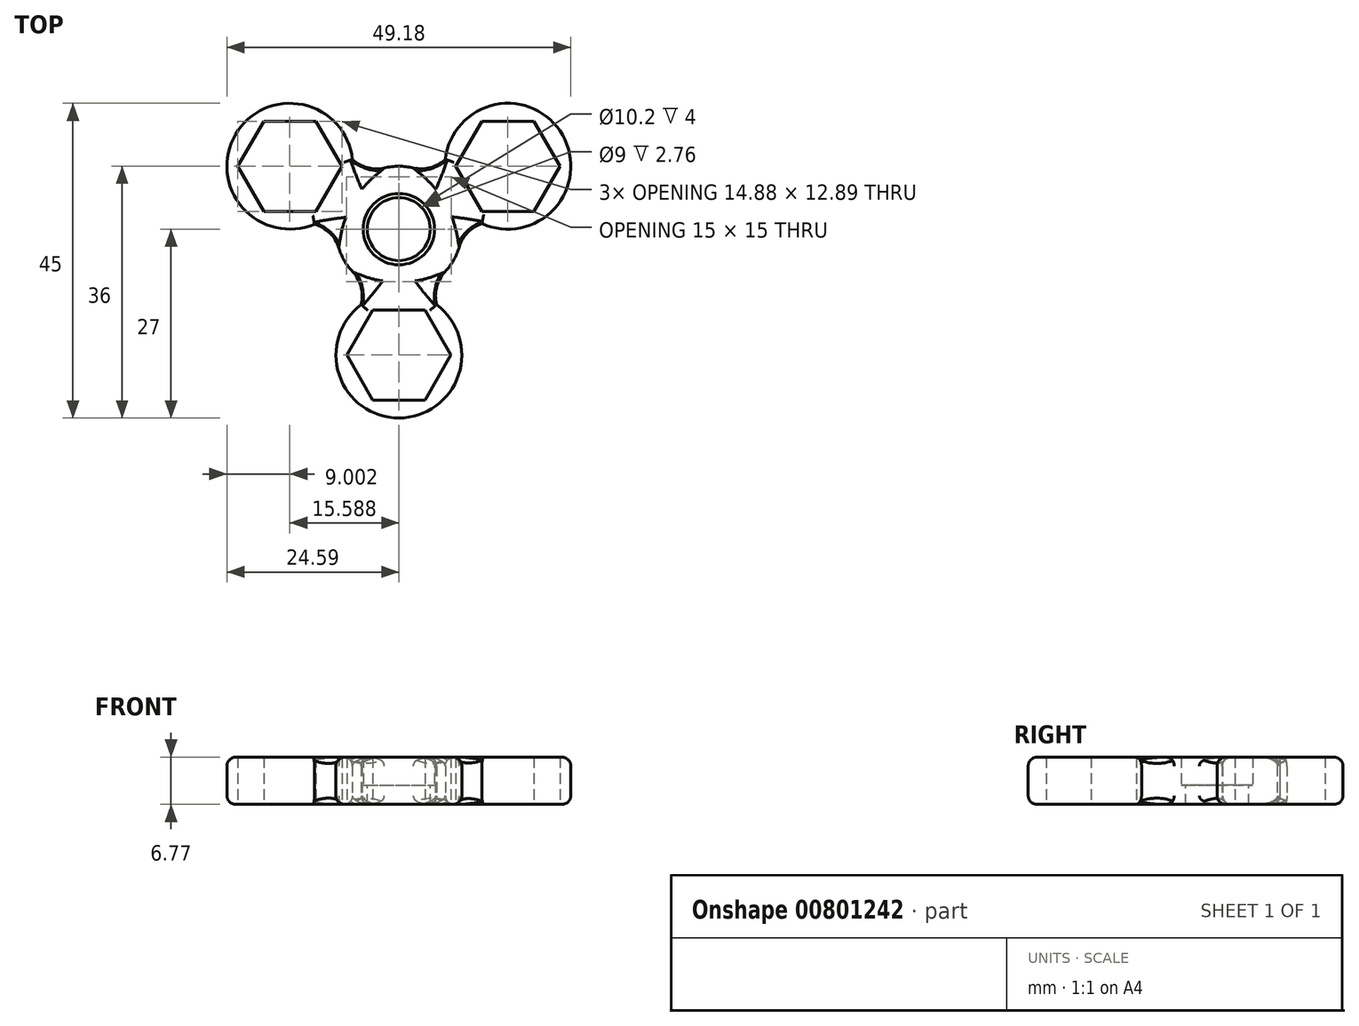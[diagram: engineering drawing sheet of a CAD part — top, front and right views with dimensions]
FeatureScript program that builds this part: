
annotation { "Feature Type Name" : "Feature", "Feature Type Description" : "" }
export const myFeature = defineFeature(function(context is Context, id is Id, definition is map)
    precondition{}
    {
        {
            var Q0;
            Q0=qCreatedBy(makeId("Top.planeOp"),FACE);
            var sketch = newSketch(context, id + "F0", { "sketchPlane" : qUnion([Q0])});
            skCircle(sketch, "E0.cCircle", {"center": v(0, 0) * mm, "radius": 9 * mm, "construction": true});
            skPoint(sketch, "E0.0.midPoint", {"position": v(0, 9) * mm});
            skCircle(sketch, "E1.cCircle", {"center": v(-15.59, 9) * mm, "radius": 6.44 * mm, "construction": true});
            skLineSegment(sketch, "E1.0", {"start": v(-19.3, 15.45) * mm, "end": v(-11.87, 15.45) * mm});
            skLineSegment(sketch, "E1.1", {"start": v(-11.87, 15.45) * mm, "end": v(-8.15, 9) * mm});
            skLineSegment(sketch, "E1.2", {"start": v(-8.15, 9) * mm, "end": v(-11.87, 2.55) * mm});
            skLineSegment(sketch, "E1.3", {"start": v(-11.87, 2.56) * mm, "end": v(-19.3, 2.56) * mm});
            skLineSegment(sketch, "E1.4", {"start": v(-19.3, 2.55) * mm, "end": v(-23.03, 9) * mm});
            skLineSegment(sketch, "E1.5", {"start": v(-23.03, 9) * mm, "end": v(-19.3, 15.45) * mm});
            skPoint(sketch, "E1.0.midPoint", {"position": v(-15.59, 15.45) * mm});
            skCircle(sketch, "E2.cCircle", {"center": v(15.59, 9) * mm, "radius": 6.44 * mm, "construction": true});
            skLineSegment(sketch, "E2.0", {"start": v(11.87, 2.55) * mm, "end": v(8.15, 9) * mm});
            skLineSegment(sketch, "E2.1", {"start": v(8.15, 9) * mm, "end": v(11.87, 15.45) * mm});
            skLineSegment(sketch, "E2.2", {"start": v(11.87, 15.45) * mm, "end": v(19.3, 15.45) * mm});
            skLineSegment(sketch, "E2.3", {"start": v(19.3, 15.45) * mm, "end": v(23.03, 9) * mm});
            skLineSegment(sketch, "E2.4", {"start": v(23.03, 9) * mm, "end": v(19.3, 2.56) * mm});
            skLineSegment(sketch, "E2.5", {"start": v(19.3, 2.56) * mm, "end": v(11.87, 2.55) * mm});
            skPoint(sketch, "E2.0.midPoint", {"position": v(10, 5.78) * mm});
            skCircle(sketch, "E3.cCircle", {"center": v(0, -18) * mm, "radius": 6.45 * mm, "construction": true});
            skLineSegment(sketch, "E3.0", {"start": v(-3.72, -11.56) * mm, "end": v(3.72, -11.56) * mm});
            skLineSegment(sketch, "E3.1", {"start": v(3.72, -11.55) * mm, "end": v(7.44, -18) * mm});
            skLineSegment(sketch, "E3.2", {"start": v(7.44, -18) * mm, "end": v(3.72, -24.44) * mm});
            skLineSegment(sketch, "E3.3", {"start": v(3.72, -24.45) * mm, "end": v(-3.72, -24.45) * mm});
            skLineSegment(sketch, "E3.4", {"start": v(-3.72, -24.45) * mm, "end": v(-7.44, -18) * mm});
            skLineSegment(sketch, "E3.5", {"start": v(-7.44, -18) * mm, "end": v(-3.72, -11.56) * mm});
            skPoint(sketch, "E3.0.midPoint", {"position": v(0, -11.56) * mm});
            skCircle(sketch, "E4", {"center": v(0, 0) * mm, "radius": 5.1 * mm});
            skLineSegment(sketch, "E5", {"start": v(-15.59, 9) * mm, "end": v(0, 0) * mm, "construction": true});
            skLineSegment(sketch, "E6", {"start": v(0, 0) * mm, "end": v(15.59, 9) * mm, "construction": true});
            skLineSegment(sketch, "E7", {"start": v(0, 0) * mm, "end": v(0, -18) * mm, "construction": true});
            skLineSegment(sketch, "E8", {"start": v(-20.06, 1.2) * mm, "end": v(0, 0) * mm, "construction": true});
            skLineSegment(sketch, "E9", {"start": v(0, 0) * mm, "end": v(-9, -18) * mm, "construction": true});
            skLineSegment(sketch, "E10", {"start": v(9, -18) * mm, "end": v(0, 0) * mm, "construction": true});
            skLineSegment(sketch, "E11", {"start": v(0, 0) * mm, "end": v(20.36, 1.37) * mm, "construction": true});
            skLineSegment(sketch, "E12", {"start": v(11.2, 16.86) * mm, "end": v(0, 0) * mm, "construction": true});
            skLineSegment(sketch, "E13", {"start": v(0, 0) * mm, "end": v(-11.22, 16.87) * mm, "construction": true});
            skLineSegment(sketch, "E14", {"start": v(-12.07, 0.72) * mm, "end": v(-8.98, 0.53) * mm});
            skLineSegment(sketch, "E15", {"start": v(-4.02, -8.05) * mm, "end": v(-5.4, -10.8) * mm});
            skLineSegment(sketch, "E16", {"start": v(4.02, -8.05) * mm, "end": v(5.4, -10.8) * mm});
            skLineSegment(sketch, "E17", {"start": v(8.98, 0.6) * mm, "end": v(11.88, 0.8) * mm});
            skLineSegment(sketch, "E18", {"start": v(4.98, 7.5) * mm, "end": v(6.64, 10) * mm});
            skLineSegment(sketch, "E19", {"start": v(-4.98, 7.5) * mm, "end": v(-6.64, 9.99) * mm});
            skArc(sketch, "E20", {"start": v(4.98, 7.5) * mm, "mid": v(0, 9) * mm, "end": v(-4.98, 7.5) * mm});
            skArc(sketch, "E21", {"start": v(8.98, 0.6) * mm, "mid": v(7.81, -4.47) * mm, "end": v(4.02, -8.05) * mm});
            skArc(sketch, "E22", {"start": v(-4.02, -8.05) * mm, "mid": v(-7.8, -4.5) * mm, "end": v(-8.98, 0.53) * mm});
            skArc(sketch, "E23", {"start": v(-6.64, 9.99) * mm, "mid": v(-23.36, 13.55) * mm, "end": v(-12.07, 0.72) * mm});
            skArc(sketch, "E24", {"start": v(6.64, 10) * mm, "mid": v(23.4, 13.45) * mm, "end": v(11.88, 0.8) * mm});
            skArc(sketch, "E25", {"start": v(5.4, -10.8) * mm, "mid": v(0, -27) * mm, "end": v(-5.4, -10.8) * mm});
            skSolve(sketch);
        }
        {
            var Q0;
            Q0 = qSketchRegion(id + "F0", true);
            extrude(context, id + "F1", {"entities" : qUnion([Q0]), "depth" : 6.75 * mm, "offsetDistance" : 25 * mm});
        }
        {
            var Q0;
            Q0=makeQuery(id+"F1.opExtrude","CAP_FACE",FACE,{"disambiguationData":[OSD([sQuery(id+"F0.wireOp",EDGE,"E1.0"),sQuery(id+"F0.wireOp",EDGE,"E1.1"),sQuery(id+"F0.wireOp",EDGE,"E1.2"),sQuery(id+"F0.wireOp",EDGE,"E1.3"),sQuery(id+"F0.wireOp",EDGE,"E1.4"),sQuery(id+"F0.wireOp",EDGE,"E1.5"),sQuery(id+"F0.wireOp",EDGE,"E2.0"),sQuery(id+"F0.wireOp",EDGE,"E2.1"),sQuery(id+"F0.wireOp",EDGE,"E2.2"),sQuery(id+"F0.wireOp",EDGE,"E2.3"),sQuery(id+"F0.wireOp",EDGE,"E2.4"),sQuery(id+"F0.wireOp",EDGE,"E2.5"),sQuery(id+"F0.wireOp",EDGE,"E3.0"),sQuery(id+"F0.wireOp",EDGE,"E3.1"),sQuery(id+"F0.wireOp",EDGE,"E3.2"),sQuery(id+"F0.wireOp",EDGE,"E3.3"),sQuery(id+"F0.wireOp",EDGE,"E3.4"),sQuery(id+"F0.wireOp",EDGE,"E3.5"),sQuery(id+"F0.wireOp",EDGE,"E4"),sQuery(id+"F0.wireOp",EDGE,"E14"),sQuery(id+"F0.wireOp",EDGE,"E15"),sQuery(id+"F0.wireOp",EDGE,"E16"),sQuery(id+"F0.wireOp",EDGE,"E17"),sQuery(id+"F0.wireOp",EDGE,"E18"),sQuery(id+"F0.wireOp",EDGE,"E19"),sQuery(id+"F0.wireOp",EDGE,"E20"),sQuery(id+"F0.wireOp",EDGE,"E21"),sQuery(id+"F0.wireOp",EDGE,"E22"),sQuery(id+"F0.wireOp",EDGE,"E23"),sQuery(id+"F0.wireOp",EDGE,"E24"),sQuery(id+"F0.wireOp",EDGE,"E25")])],"isStart":false});
            var sketch = newSketch(context, id + "F2", { "sketchPlane" : qUnion([Q0])});
            skCircle(sketch, "E26", {"center": v(0, 0) * mm, "radius": 7.5 * mm});
            skSolve(sketch);
        }
        {
            var Q0;
            Q0 = qSketchRegion(id + "F2", true);
            extrude(context, id + "F3", {"entities" : qUnion([Q0]), "operationType" : NewBodyOperationType.REMOVE, "oppositeDirection" : true, "depth" : 1.38 * mm, "offsetDistance" : 25 * mm});
        }
        {
            var Q0;
            Q0=makeQuery(id+"F1.opExtrude","CAP_FACE",FACE,{"disambiguationData":[OSD([sQuery(id+"F0.wireOp",EDGE,"E1.0"),sQuery(id+"F0.wireOp",EDGE,"E1.1"),sQuery(id+"F0.wireOp",EDGE,"E1.2"),sQuery(id+"F0.wireOp",EDGE,"E1.3"),sQuery(id+"F0.wireOp",EDGE,"E1.4"),sQuery(id+"F0.wireOp",EDGE,"E1.5"),sQuery(id+"F0.wireOp",EDGE,"E2.0"),sQuery(id+"F0.wireOp",EDGE,"E2.1"),sQuery(id+"F0.wireOp",EDGE,"E2.2"),sQuery(id+"F0.wireOp",EDGE,"E2.3"),sQuery(id+"F0.wireOp",EDGE,"E2.4"),sQuery(id+"F0.wireOp",EDGE,"E2.5"),sQuery(id+"F0.wireOp",EDGE,"E3.0"),sQuery(id+"F0.wireOp",EDGE,"E3.1"),sQuery(id+"F0.wireOp",EDGE,"E3.2"),sQuery(id+"F0.wireOp",EDGE,"E3.3"),sQuery(id+"F0.wireOp",EDGE,"E3.4"),sQuery(id+"F0.wireOp",EDGE,"E3.5"),sQuery(id+"F0.wireOp",EDGE,"E4"),sQuery(id+"F0.wireOp",EDGE,"E14"),sQuery(id+"F0.wireOp",EDGE,"E15"),sQuery(id+"F0.wireOp",EDGE,"E16"),sQuery(id+"F0.wireOp",EDGE,"E17"),sQuery(id+"F0.wireOp",EDGE,"E18"),sQuery(id+"F0.wireOp",EDGE,"E19"),sQuery(id+"F0.wireOp",EDGE,"E20"),sQuery(id+"F0.wireOp",EDGE,"E21"),sQuery(id+"F0.wireOp",EDGE,"E22"),sQuery(id+"F0.wireOp",EDGE,"E23"),sQuery(id+"F0.wireOp",EDGE,"E24"),sQuery(id+"F0.wireOp",EDGE,"E25")])],"isStart":true});
            var sketch = newSketch(context, id + "F4", { "sketchPlane" : qUnion([Q0])});
            skCircle(sketch, "E27", {"center": v(0, 0) * mm, "radius": 7.5 * mm});
            skSolve(sketch);
        }
        {
            var Q0;
            Q0 = qSketchRegion(id + "F4", true);
            extrude(context, id + "F5", {"entities" : qUnion([Q0]), "operationType" : NewBodyOperationType.REMOVE, "oppositeDirection" : true, "depth" : 1.38 * mm, "offsetDistance" : 25 * mm});
        }
        {
            var Q0;
            Q0=makeQuery(id+"F1.opExtrude","CAP_EDGE",EDGE,{"disambiguationData":[OSD([sQuery(id+"F0.wireOp",EDGE,"E23")])],"isStart":false});
            var Q1;
            Q1=makeQuery(id+"F1.opExtrude","CAP_EDGE",EDGE,{"disambiguationData":[OSD([sQuery(id+"F0.wireOp",EDGE,"E19")])],"isStart":false});
            var Q2;
            Q2=makeQuery(id+"F1.opExtrude","CAP_EDGE",EDGE,{"disambiguationData":[OSD([sQuery(id+"F0.wireOp",EDGE,"E20")])],"isStart":false});
            var Q3;
            Q3=makeQuery(id+"F1.opExtrude","CAP_EDGE",EDGE,{"disambiguationData":[OSD([sQuery(id+"F0.wireOp",EDGE,"E18")])],"isStart":false});
            var Q4;
            Q4=makeQuery(id+"F1.opExtrude","CAP_EDGE",EDGE,{"disambiguationData":[OSD([sQuery(id+"F0.wireOp",EDGE,"E24")])],"isStart":false});
            var Q5;
            Q5=makeQuery(id+"F1.opExtrude","CAP_EDGE",EDGE,{"disambiguationData":[OSD([sQuery(id+"F0.wireOp",EDGE,"E17")])],"isStart":false});
            var Q6;
            Q6=makeQuery(id+"F1.opExtrude","CAP_EDGE",EDGE,{"disambiguationData":[OSD([sQuery(id+"F0.wireOp",EDGE,"E21")])],"isStart":false});
            var Q7;
            Q7=makeQuery(id+"F1.opExtrude","CAP_EDGE",EDGE,{"disambiguationData":[OSD([sQuery(id+"F0.wireOp",EDGE,"E16")])],"isStart":false});
            var Q8;
            Q8=makeQuery(id+"F1.opExtrude","CAP_EDGE",EDGE,{"disambiguationData":[OSD([sQuery(id+"F0.wireOp",EDGE,"E25")])],"isStart":false});
            var Q9;
            Q9=makeQuery(id+"F1.opExtrude","CAP_EDGE",EDGE,{"disambiguationData":[OSD([sQuery(id+"F0.wireOp",EDGE,"E15")])],"isStart":false});
            var Q10;
            Q10=makeQuery(id+"F1.opExtrude","CAP_EDGE",EDGE,{"disambiguationData":[OSD([sQuery(id+"F0.wireOp",EDGE,"E22")])],"isStart":false});
            var Q11;
            Q11=makeQuery(id+"F1.opExtrude","CAP_EDGE",EDGE,{"disambiguationData":[OSD([sQuery(id+"F0.wireOp",EDGE,"E14")])],"isStart":false});
            var Q12;
            Q12=makeQuery(id+"F1.opExtrude","CAP_EDGE",EDGE,{"disambiguationData":[OSD([sQuery(id+"F0.wireOp",EDGE,"E20")])],"isStart":true});
            var Q13;
            Q13=makeQuery(id+"F1.opExtrude","CAP_EDGE",EDGE,{"disambiguationData":[OSD([sQuery(id+"F0.wireOp",EDGE,"E19")])],"isStart":true});
            var Q14;
            Q14=makeQuery(id+"F1.opExtrude","CAP_EDGE",EDGE,{"disambiguationData":[OSD([sQuery(id+"F0.wireOp",EDGE,"E23")])],"isStart":true});
            var Q15;
            Q15=makeQuery(id+"F1.opExtrude","CAP_EDGE",EDGE,{"disambiguationData":[OSD([sQuery(id+"F0.wireOp",EDGE,"E14")])],"isStart":true});
            var Q16;
            Q16=makeQuery(id+"F1.opExtrude","CAP_EDGE",EDGE,{"disambiguationData":[OSD([sQuery(id+"F0.wireOp",EDGE,"E22")])],"isStart":true});
            var Q17;
            Q17=makeQuery(id+"F1.opExtrude","CAP_EDGE",EDGE,{"disambiguationData":[OSD([sQuery(id+"F0.wireOp",EDGE,"E15")])],"isStart":true});
            var Q18;
            Q18=makeQuery(id+"F1.opExtrude","CAP_EDGE",EDGE,{"disambiguationData":[OSD([sQuery(id+"F0.wireOp",EDGE,"E25")])],"isStart":true});
            var Q19;
            Q19=makeQuery(id+"F1.opExtrude","CAP_EDGE",EDGE,{"disambiguationData":[OSD([sQuery(id+"F0.wireOp",EDGE,"E16")])],"isStart":true});
            var Q20;
            Q20=makeQuery(id+"F1.opExtrude","CAP_EDGE",EDGE,{"disambiguationData":[OSD([sQuery(id+"F0.wireOp",EDGE,"E21")])],"isStart":true});
            var Q21;
            Q21=makeQuery(id+"F1.opExtrude","CAP_EDGE",EDGE,{"disambiguationData":[OSD([sQuery(id+"F0.wireOp",EDGE,"E17")])],"isStart":true});
            var Q22;
            Q22=makeQuery(id+"F1.opExtrude","CAP_EDGE",EDGE,{"disambiguationData":[OSD([sQuery(id+"F0.wireOp",EDGE,"E24")])],"isStart":true});
            var Q23;
            Q23=makeQuery(id+"F1.opExtrude","CAP_EDGE",EDGE,{"disambiguationData":[OSD([sQuery(id+"F0.wireOp",EDGE,"E18")])],"isStart":true});
            fillet(context, id + "F6", {"entities" : qUnion([Q0, Q1, Q2, Q3, Q4, Q5, Q6, Q7, Q8, Q9, Q10, Q11, Q12, Q13, Q14, Q15, Q16, Q17, Q18, Q19, Q20, Q21, Q22, Q23]), "radius" : 1.25 * mm, "tangentPropagation" : true, "allowEdgeOverflow" : false});
        }
        {
            var Q0;
            Q0=makeQuery(id+"F1.opExtrude","SWEPT_EDGE",EDGE,{"disambiguationData":[OSD([sQuery(id+"F0.wireOp",EDGE,"E16"),sQuery(id+"F0.wireOp",EDGE,"E21")])]});
            var Q1;
            Q1=makeQuery(id+"F1.opExtrude","SWEPT_EDGE",EDGE,{"disambiguationData":[OSD([sQuery(id+"F0.wireOp",EDGE,"E17"),sQuery(id+"F0.wireOp",EDGE,"E21")])]});
            var Q2;
            Q2=makeQuery(id+"F1.opExtrude","SWEPT_EDGE",EDGE,{"disambiguationData":[OSD([sQuery(id+"F0.wireOp",EDGE,"E18"),sQuery(id+"F0.wireOp",EDGE,"E20")])]});
            var Q3;
            Q3=makeQuery(id+"F1.opExtrude","SWEPT_EDGE",EDGE,{"disambiguationData":[OSD([sQuery(id+"F0.wireOp",EDGE,"E19"),sQuery(id+"F0.wireOp",EDGE,"E20")])]});
            var Q4;
            Q4=makeQuery(id+"F1.opExtrude","SWEPT_EDGE",EDGE,{"disambiguationData":[OSD([sQuery(id+"F0.wireOp",EDGE,"E15"),sQuery(id+"F0.wireOp",EDGE,"E22")])]});
            var Q5;
            Q5=makeQuery(id+"F1.opExtrude","SWEPT_EDGE",EDGE,{"disambiguationData":[OSD([sQuery(id+"F0.wireOp",EDGE,"E14"),sQuery(id+"F0.wireOp",EDGE,"E22")])]});
            fillet(context, id + "F7", {"entities" : qUnion([Q0, Q1, Q2, Q3, Q4, Q5]), "radius" : 5 * mm, "tangentPropagation" : true, "allowEdgeOverflow" : false});
        }
        {
            var Q0;
            Q0=makeQuery(id+"F3.boolean.opBoolean","COPY",FACE,{"derivedFrom":makeQuery(id+"F3.opExtrude","CAP_FACE",FACE,{"disambiguationData":[OSD([sQuery(id+"F2.wireOp",EDGE,"E26")])],"isStart":false})});
            extrude(context, id + "F8", {"entities" : qUnion([Q0]), "operationType" : NewBodyOperationType.ADD, "depth" : 1.38 * mm, "offsetDistance" : 25 * mm});
        }
        {
            var Q0;
            Q0=makeQuery(id+"F5.boolean.opBoolean","COPY",FACE,{"derivedFrom":makeQuery(id+"F5.opExtrude","CAP_FACE",FACE,{"disambiguationData":[OSD([sQuery(id+"F4.wireOp",EDGE,"E27")])],"isStart":false})});
            extrude(context, id + "F9", {"entities" : qUnion([Q0]), "operationType" : NewBodyOperationType.REMOVE, "oppositeDirection" : true, "depth" : 1.38 * mm, "offsetDistance" : 25 * mm});
        }
        {
            var Q0;
            Q0=makeQuery(id+"F9.boolean.opBoolean","COPY",FACE,{"derivedFrom":makeQuery(id+"F9.opExtrude","CAP_FACE",FACE,{"disambiguationData":[OSD([sQuery(id+"F4.wireOp",EDGE,"E27")])],"isStart":false})});
            var sketch = newSketch(context, id + "F10", { "sketchPlane" : qUnion([Q0])});
            skCircle(sketch, "E28", {"center": v(0, 0) * mm, "radius": 4.5 * mm});
            skSolve(sketch);
        }
        {
            var Q0;
            Q0=makeQuery(id+"F10.imprint","IMPRINT",FACE,{"disambiguationData":[TD([[makeQuery(id+"F10.imprint","IMPRINT",EDGE,{"derivedFrom":sQuery(id+"F10.wireOp",EDGE,"E28")}),-1.0]])]});
            var Q1;
            {var subQ0=sQuery(id+"F4.wireOp",EDGE,"E27");Q1=makeQuery(id+"F10.imprint","IMPRINT",FACE,{"disambiguationData":[TD([[makeQuery(id+"F10.imprint","IMPRINT",EDGE,{"derivedFrom":makeQuery(id+"F9.boolean.opBoolean","COPY",EDGE,{"derivedFrom":makeQuery(id+"F9.opExtrude","CAP_EDGE",EDGE,{"disambiguationData":[OSD([subQ0])],"isStart":false})})}),1.0]])]});}
            extrude(context, id + "F11", {"entities" : qUnion([Q0, Q1]), "operationType" : NewBodyOperationType.ADD, "depth" : 1.38 * mm, "offsetDistance" : 25 * mm});
        }
        {
            var Q0;
            Q0=makeQuery(id+"F11.opExtrude","CAP_FACE",FACE,{"disambiguationData":[OSD([sQuery(id+"F4.wireOp",EDGE,"E27"),sQuery(id+"F10.wireOp",EDGE,"E28")])],"isStart":false});
            extrude(context, id + "F12", {"entities" : qUnion([Q0]), "operationType" : NewBodyOperationType.ADD, "depth" : 1.38 * mm, "offsetDistance" : 25 * mm});
        }
    });
